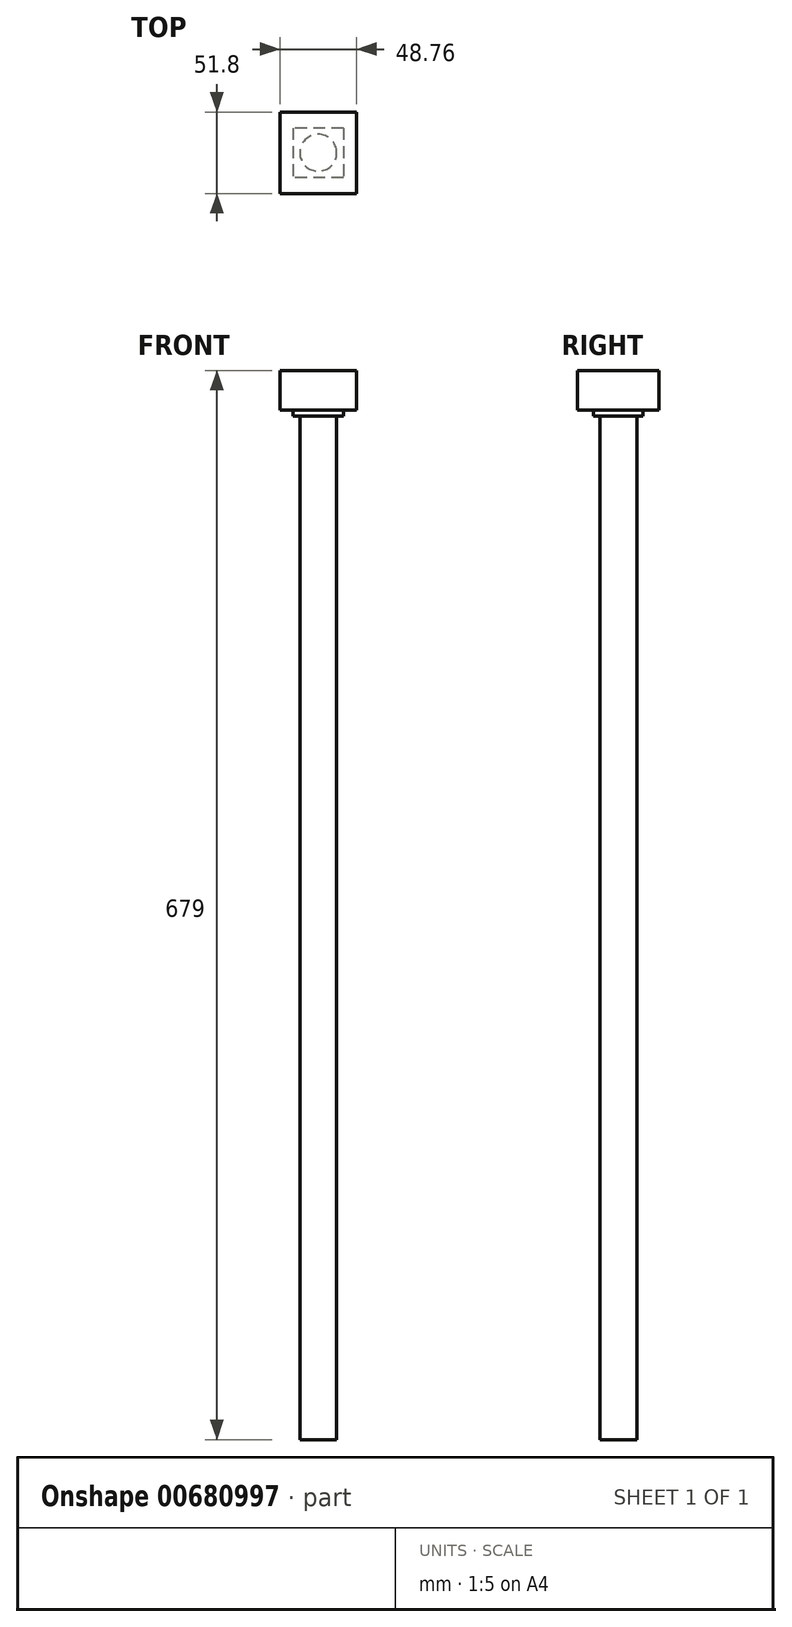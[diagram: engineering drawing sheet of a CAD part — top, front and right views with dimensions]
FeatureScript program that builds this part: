
annotation { "Feature Type Name" : "Feature", "Feature Type Description" : "" }
export const myFeature = defineFeature(function(context is Context, id is Id, definition is map)
    precondition{}
    {
        {
            var Q0;
            Q0=qCreatedBy(makeId("Top.planeOp"),FACE);
            var sketch = newSketch(context, id + "F0", { "sketchPlane" : qUnion([Q0])});
            skLineSegment(sketch, "E0.bottom", {"start": v(-24.38, -25.9) * mm, "end": v(24.38, -25.9) * mm});
            skLineSegment(sketch, "E0.top", {"start": v(-24.38, 25.9) * mm, "end": v(24.38, 25.9) * mm});
            skLineSegment(sketch, "E0.left", {"start": v(-24.38, -25.9) * mm, "end": v(-24.38, 25.9) * mm});
            skLineSegment(sketch, "E0.right", {"start": v(24.38, -25.9) * mm, "end": v(24.38, 25.9) * mm});
            skPoint(sketch, "E0.middle", {"position": v(0, 0) * mm});
            skSolve(sketch);
        }
        {
            var Q0;
            Q0 = qSketchRegion(id + "F0", true);
            extrude(context, id + "F1", {"entities" : qUnion([Q0]), "depth" : 25 * mm, "offsetDistance" : 25 * mm});
        }
        {
            var Q0;
            Q0=makeQuery(id+"F1.opExtrude","CAP_FACE",FACE,{"disambiguationData":[OSD([sQuery(id+"F0.wireOp",EDGE,"E0.bottom"),sQuery(id+"F0.wireOp",EDGE,"E0.top"),sQuery(id+"F0.wireOp",EDGE,"E0.left"),sQuery(id+"F0.wireOp",EDGE,"E0.right")])],"isStart":true});
            var sketch = newSketch(context, id + "F2", { "sketchPlane" : qUnion([Q0])});
            skLineSegment(sketch, "E1.bottom", {"start": v(15.88, -15.7) * mm, "end": v(-15.88, -15.7) * mm});
            skLineSegment(sketch, "E1.top", {"start": v(15.88, 15.7) * mm, "end": v(-15.88, 15.7) * mm});
            skLineSegment(sketch, "E1.left", {"start": v(15.88, -15.7) * mm, "end": v(15.88, 15.7) * mm});
            skLineSegment(sketch, "E1.right", {"start": v(-15.88, -15.7) * mm, "end": v(-15.88, 15.7) * mm});
            skPoint(sketch, "E1.middle", {"position": v(0, 0) * mm});
            skSolve(sketch);
        }
        {
            var Q0;
            Q0 = qSketchRegion(id + "F2", true);
            extrude(context, id + "F3", {"entities" : qUnion([Q0]), "operationType" : NewBodyOperationType.ADD, "depth" : 4 * mm, "offsetDistance" : 25 * mm});
        }
        {
            var Q0;
            Q0=makeQuery(id+"F3.opExtrude","CAP_FACE",FACE,{"disambiguationData":[OSD([sQuery(id+"F2.wireOp",EDGE,"E1.bottom"),sQuery(id+"F2.wireOp",EDGE,"E1.top"),sQuery(id+"F2.wireOp",EDGE,"E1.left"),sQuery(id+"F2.wireOp",EDGE,"E1.right")])],"isStart":false});
            var sketch = newSketch(context, id + "F4", { "sketchPlane" : qUnion([Q0])});
            skCircle(sketch, "E2", {"center": v(0, 0) * mm, "radius": 11.71 * mm});
            skSolve(sketch);
        }
        {
            var Q0;
            Q0 = qSketchRegion(id + "F4", true);
            extrude(context, id + "F5", {"entities" : qUnion([Q0]), "operationType" : NewBodyOperationType.ADD, "depth" : 650 * mm, "offsetDistance" : 25 * mm});
        }
    });
